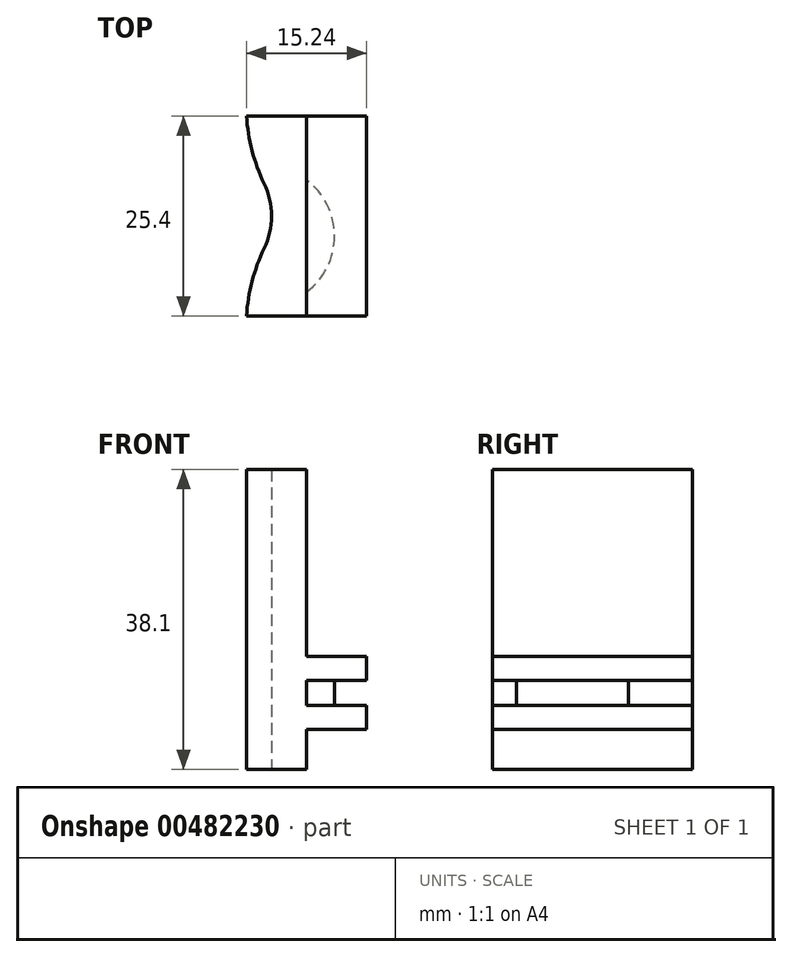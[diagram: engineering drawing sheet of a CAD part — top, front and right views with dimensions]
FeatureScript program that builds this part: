
annotation { "Feature Type Name" : "Feature", "Feature Type Description" : "" }
export const myFeature = defineFeature(function(context is Context, id is Id, definition is map)
    precondition{}
    {
        {
            var Q0;
            Q0=qCreatedBy(makeId("Top.planeOp"),FACE);
            var sketch = newSketch(context, id + "F0", { "sketchPlane" : qUnion([Q0])});
            skLineSegment(sketch, "E0.bottom", {"start": v(3.8, -12.7) * mm, "end": v(-3.81, -12.7) * mm});
            skLineSegment(sketch, "E0.top", {"start": v(3.8, 12.7) * mm, "end": v(-3.81, 12.7) * mm});
            skLineSegment(sketch, "E0.left", {"start": v(3.8, -12.7) * mm, "end": v(3.8, 12.7) * mm});
            skLineSegment(sketch, "E0.right", {"start": v(-3.81, -12.7) * mm, "end": v(-3.81, 12.7) * mm});
            skPoint(sketch, "E0.middle", {"position": v(0, 0) * mm});
            skCircle(sketch, "E1", {"center": v(-10.16, 0) * mm, "radius": 9.52 * mm});
            skSolve(sketch);
        }
        {
            var Q0;
            {var subQ1=sQuery(id+"F0.wireOp",EDGE,"E0.bottom");Q0=makeQuery(id+"F0.imprint","IMPRINT",FACE,{"disambiguationData":[TD([[makeQuery(id+"F0.imprint","IMPRINT",EDGE,{"derivedFrom":subQ1}),-1.0]])]});}
            extrude(context, id + "F1", {"entities" : qUnion([Q0]), "depth" : 25.4 * mm, "offsetDistance" : 25.4 * mm});
        }
        {
            var Q0;
            {var subQ0=sQuery(id+"F0.wireOp",EDGE,"E1");var subQ1=sQuery(id+"F0.wireOp",EDGE,"E0.right");Q0=makeQuery(id+"F1.opExtrude","SWEPT_EDGE",EDGE,{"disambiguationData":[OSD([subQ1,subQ0]),TDD([makeQuery(id+"F0.imprint","INTERSECT",VERTEX,{"disambiguationData":[OD(1.0)],"derivedFrom":[subQ1,subQ0]})])]});}
            var Q1;
            {var subQ0=sQuery(id+"F0.wireOp",EDGE,"E1");var subQ1=sQuery(id+"F0.wireOp",EDGE,"E0.right");Q1=makeQuery(id+"F1.opExtrude","SWEPT_EDGE",EDGE,{"disambiguationData":[OSD([subQ1,subQ0]),TDD([makeQuery(id+"F0.imprint","INTERSECT",VERTEX,{"disambiguationData":[OD(0.0)],"derivedFrom":[subQ1,subQ0]})])]});}
            fillet(context, id + "F2", {"entities" : qUnion([Q0, Q1]), "radius" : 22.86 * mm, "tangentPropagation" : true, "allowEdgeOverflow" : false});
        }
        {
            var Q0;
            Q0=makeQuery(id+"F1.opExtrude","CAP_FACE",FACE,{"disambiguationData":[OSD([sQuery(id+"F0.wireOp",EDGE,"E0.bottom"),sQuery(id+"F0.wireOp",EDGE,"E0.top"),sQuery(id+"F0.wireOp",EDGE,"E0.left"),sQuery(id+"F0.wireOp",EDGE,"E0.right"),sQuery(id+"F0.wireOp",EDGE,"E1")])],"isStart":false});
            extrude(context, id + "F3", {"entities" : qUnion([Q0]), "operationType" : NewBodyOperationType.ADD, "depth" : 10.16 * mm, "offsetDistance" : 25.4 * mm});
        }
        {
            var Q0;
            Q0=makeQuery(id+"F3.opExtrude","CAP_FACE",FACE,{"disambiguationData":[OSD([sQuery(id+"F0.wireOp",EDGE,"E0.bottom"),sQuery(id+"F0.wireOp",EDGE,"E0.top"),sQuery(id+"F0.wireOp",EDGE,"E0.left"),sQuery(id+"F0.wireOp",EDGE,"E0.right"),sQuery(id+"F0.wireOp",EDGE,"E1")])],"isStart":false});
            extrude(context, id + "F4", {"entities" : qUnion([Q0]), "operationType" : NewBodyOperationType.ADD, "depth" : 2.54 * mm, "offsetDistance" : 25.4 * mm});
        }
        {
            var Q0;
            {var subQ0=sQuery(id+"F0.wireOp",EDGE,"E0.left");Q0=makeQuery(id+"F4.boolean.opBoolean","MERGE",FACE,{"derivedFrom":[makeQuery(id+"F3.boolean.opBoolean","MERGE",FACE,{"derivedFrom":[makeQuery(id+"F1.opExtrude","SWEPT_FACE",FACE,{"disambiguationData":[OSD([subQ0])]}),makeQuery(id+"F3.opExtrude","SWEPT_FACE",FACE,{"disambiguationData":[OSD([subQ0])]})]}),makeQuery(id+"F4.opExtrude","SWEPT_FACE",FACE,{"disambiguationData":[OSD([subQ0])]})]});}
            var sketch = newSketch(context, id + "F5", { "sketchPlane" : qUnion([Q0])});
            skLineSegment(sketch, "E2.bottom", {"start": v(-12.7, 5.08) * mm, "end": v(12.7, 5.08) * mm});
            skLineSegment(sketch, "E2.top", {"start": v(-12.7, 8.13) * mm, "end": v(12.7, 8.13) * mm});
            skLineSegment(sketch, "E2.left", {"start": v(-12.7, 5.08) * mm, "end": v(-12.7, 8.13) * mm});
            skLineSegment(sketch, "E2.right", {"start": v(12.7, 5.08) * mm, "end": v(12.7, 8.13) * mm});
            skLineSegment(sketch, "E3.bottom", {"start": v(12.7, 11.3) * mm, "end": v(-12.7, 11.3) * mm});
            skLineSegment(sketch, "E3.top", {"start": v(12.7, 14.35) * mm, "end": v(-12.7, 14.35) * mm});
            skLineSegment(sketch, "E3.left", {"start": v(12.7, 11.3) * mm, "end": v(12.7, 14.35) * mm});
            skLineSegment(sketch, "E3.right", {"start": v(-12.7, 11.3) * mm, "end": v(-12.7, 14.35) * mm});
            skSolve(sketch);
        }
        {
            var Q0;
            Q0=makeQuery(id+"F5.imprint","IMPRINT",FACE,{"disambiguationData":[TD([[makeQuery(id+"F5.imprint","IMPRINT",EDGE,{"derivedFrom":sQuery(id+"F5.wireOp",EDGE,"E3.bottom")}),-1.0]])]});
            var Q1;
            Q1=makeQuery(id+"F5.imprint","IMPRINT",FACE,{"disambiguationData":[TD([[makeQuery(id+"F5.imprint","IMPRINT",EDGE,{"derivedFrom":sQuery(id+"F5.wireOp",EDGE,"E2.bottom")}),1.0]])]});
            extrude(context, id + "F6", {"entities" : qUnion([Q0, Q1]), "operationType" : NewBodyOperationType.ADD, "depth" : 7.62 * mm, "offsetDistance" : 25.4 * mm});
        }
        {
            var Q0;
            Q0=makeQuery(id+"F6.opExtrude","SWEPT_FACE",FACE,{"disambiguationData":[OSD([sQuery(id+"F5.wireOp",EDGE,"E2.top")])]});
            var sketch = newSketch(context, id + "F7", { "sketchPlane" : qUnion([Q0])});
            skCircle(sketch, "E4", {"center": v(-1.52, -2.54) * mm, "radius": 8.9 * mm});
            skSolve(sketch);
        }
        {
            var Q0;
            {var subQ0=sQuery(id+"F7.wireOp",EDGE,"E4");var subQ1=makeQuery(id+"F6.opExtrude","CAP_EDGE",EDGE,{"disambiguationData":[OSD([sQuery(id+"F5.wireOp",EDGE,"E2.top")])],"isStart":true});var subQ2=makeQuery(id+"F7.imprint","INTERSECT",VERTEX,{"disambiguationData":[OD(0.0)],"derivedFrom":[subQ1,subQ0]});Q0=makeQuery(id+"F7.imprint","IMPRINT",FACE,{"disambiguationData":[TD([[makeQuery(id+"F7.imprint","IMPRINT",EDGE,{"disambiguationData":[TD([[subQ2,-1.0]])],"derivedFrom":subQ0}),1.0]])]});}
            extrude(context, id + "F8", {"entities" : qUnion([Q0]), "operationType" : NewBodyOperationType.ADD, "depth" : 5.08 * mm, "offsetDistance" : 25.4 * mm});
        }
    });
